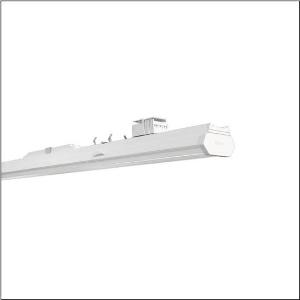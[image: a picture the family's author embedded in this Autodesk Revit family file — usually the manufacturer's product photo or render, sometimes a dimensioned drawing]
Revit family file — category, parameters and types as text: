
# Revit family: licross_r__21_protected_mo_52tp12dn48xg_9fce
name_source: partatom
category: Lighting Fixtures
units: mm (PartAtom-declared; Revit-internal decimal feet)

## family parameters
Cut with Voids When Loaded = No
Host = Face
Light Source = No
Part Type = Normal
Room Calculation Point = No
Round Connector Dimension = Use Diameter
Shared = No

## types (1)
- --- (1 x LED, 8000 lm, 45.3 W, 4000K)
    Apparent Load = 45 VA
    CIE Flux Codes = 73 92 98 99 100
    Color Rendering = 80
    Color Temperature = 4000K
    Default Elevation = 1800 mm
    Description = Licross® 21 Protected MO, luminaire insert, of sheet steel, galvanised, coil coated, white, length: 1.500mm, width: 90mm, height: 103mm, LED rated luminous flux: 8.000lm, light colour: 840, SDCM (Standard Deviation of Colour Matching)MacAdam ≤ 3 SDCM (initial), control gear: DALI 2, with plug, 5-pole, with phase selection, mains connection: 220..240V, AC, 50/60Hz, rated input power: 45W, internal wiring halogen-free, primary light control with lens, of plastic, primary optical cover: cover, of PMMA, light emission: direct distribution, primary light characteristic: symmetric, protection rating (complete): IP64, insulation class (complete): insulation class I (protective earthing), certification: CE, ENEC, VDE, UKCA, protection symbol: D if used in an environment with conductive dust loads with corresponding accessories, impact resistance: IK06, permissible ambient temperature for indoor applications: -25..+45°C, corresponds to IFS (International Featured Standards) requirements for safety and quality in the food industry, reducing of maximum allowable ambient temperature of 5°C with ceiling mounting, LABS conformity tested according to VDMA 24364:2018-05, packaging unit: 1 piece
    Height = 92 mm
    Lamp = 1 x LED
    Lamp Light Flux = 8000 lm
    Lamp Power = 45.3 W
    Lamp count = 1
    Length = 1500 mm
    Luminous efficacy = 177 lm/W
    Manufacturer = Siteco
    ModVariant = No
    Model = 52TP12DN48XG
    Mounting Place = Ceiling
    Mounting Type = Pendant
    Number of Poles = 1
    OnlyDefault = Yes
    Power Factor = 1
    Product Name = Licross® 21 Protected MO
    Product group = luminaire insert | ceiling pendant
    ProductGroupID = 901
    Protection Class = Protection class I
    Protection Degree = IP 64
    RLX_Detail_Level = 1
    RLX_Emergency_Light_Flux = 0 lm
    RLX_Emergency_Type = 0
    RLX_Emergency_Type_DB = No
    RlxData = <blob elided: 24425 chars, md5=1fa28680>
    Socket = socket
    Standby Power = 0 W
    System Light Flux = 8000 lm
    System Power = 45 W
    Type Comments = factory setting: luminous flux: 100 % | dim-lin: 254 | 305 mA
    Type Image = l_1256148.jpg
    URL = http://relux.com
    VarID = @adj_132585
    Voltage = 0 V
    Weight = 0.00 kg
    Width = 88 mm

## geometry (parser evidence)
native form markers: Blend x4, Sweep x11
no freeform markers — native parametric forms only
